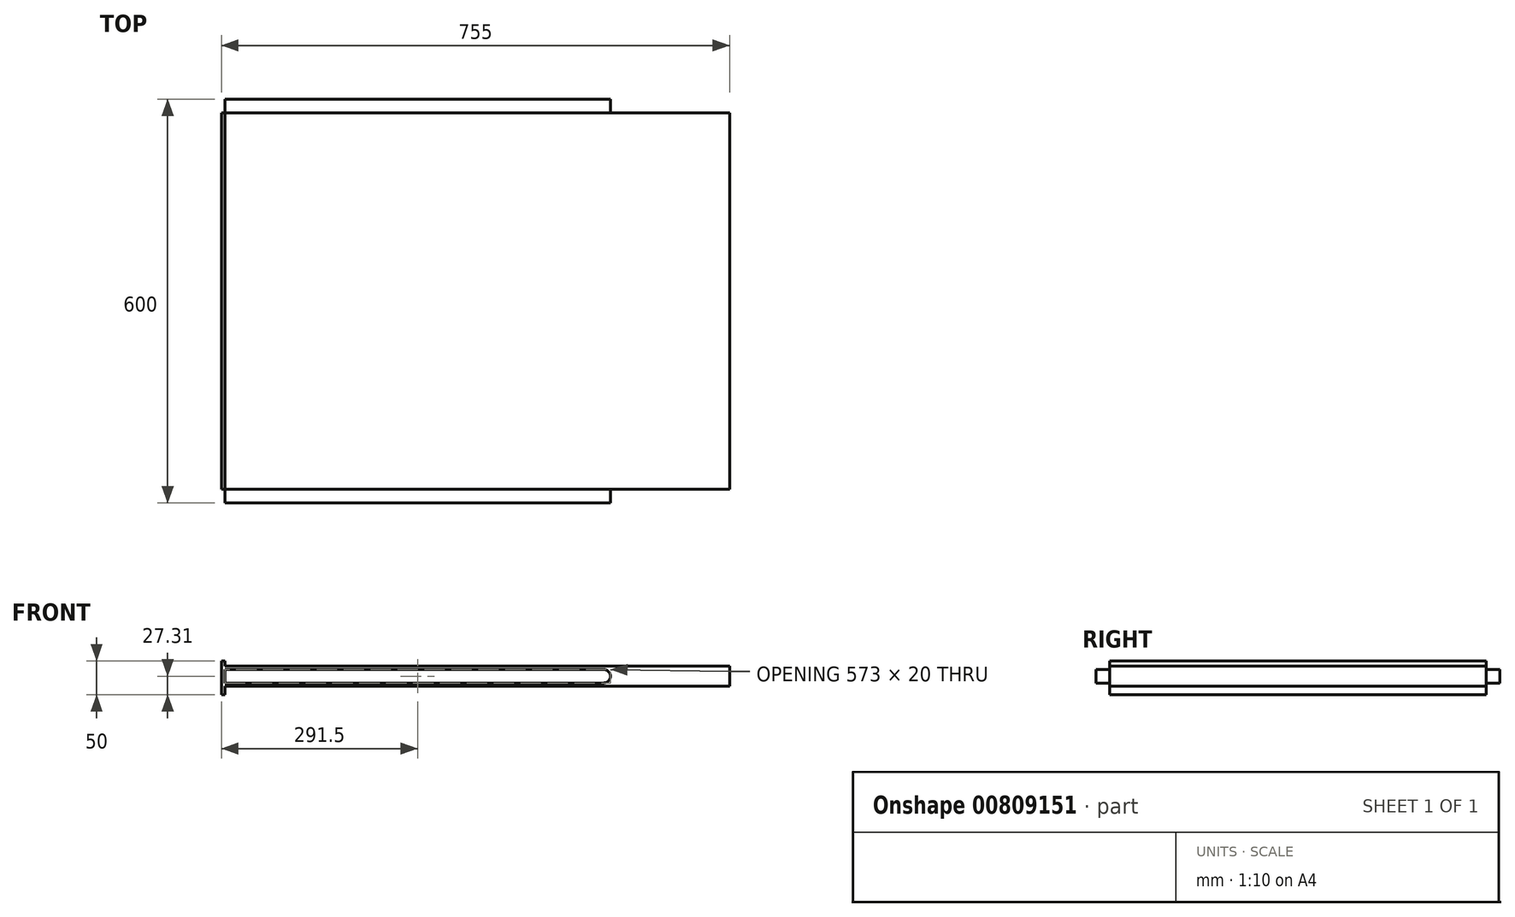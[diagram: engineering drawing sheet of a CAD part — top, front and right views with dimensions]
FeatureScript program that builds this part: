
annotation { "Feature Type Name" : "Feature", "Feature Type Description" : "" }
export const myFeature = defineFeature(function(context is Context, id is Id, definition is map)
    precondition{}
    {
        {
            var Q0;
            Q0=qCreatedBy(makeId("Top.planeOp"),FACE);
            var sketch = newSketch(context, id + "F0", { "sketchPlane" : qUnion([Q0])});
            skLineSegment(sketch, "E0.bottom", {"start": v(375, -280) * mm, "end": v(-375, -280) * mm});
            skLineSegment(sketch, "E0.top", {"start": v(375, 280) * mm, "end": v(-375, 280) * mm});
            skLineSegment(sketch, "E0.left", {"start": v(375, -280) * mm, "end": v(375, 280) * mm});
            skLineSegment(sketch, "E0.right", {"start": v(-375, -280) * mm, "end": v(-375, 280) * mm});
            skPoint(sketch, "E0.middle", {"position": v(0, 0) * mm});
            skSolve(sketch);
        }
        {
            var Q0;
            Q0 = qSketchRegion(id + "F0", true);
            extrude(context, id + "F1", {"entities" : qUnion([Q0]), "depth" : 30 * mm, "offsetDistance" : 25 * mm});
        }
        {
            var Q0;
            Q0=makeQuery(id+"F1.opExtrude","SWEPT_FACE",FACE,{"disambiguationData":[OSD([sQuery(id+"F0.wireOp",EDGE,"E0.bottom")])]});
            var sketch = newSketch(context, id + "F2", { "sketchPlane" : qUnion([Q0])});
            skLineSegment(sketch, "E1", {"start": v(-375, 5) * mm, "end": v(188, 5) * mm});
            skLineSegment(sketch, "E2", {"start": v(-375, 25) * mm, "end": v(188, 25) * mm});
            skArc(sketch, "E3", {"start": v(188, 25) * mm, "mid": v(198, 15) * mm, "end": v(188, 5) * mm});
            skSolve(sketch);
        }
        {
            var Q0;
            Q0=makeQuery(id+"F1.opExtrude","SWEPT_FACE",FACE,{"disambiguationData":[OSD([sQuery(id+"F0.wireOp",EDGE,"E0.top")])]});
            var sketch = newSketch(context, id + "F3", { "sketchPlane" : qUnion([Q0])});
            skLineSegment(sketch, "E4", {"start": v(375, 5) * mm, "end": v(-188, 5) * mm});
            skLineSegment(sketch, "E5", {"start": v(375, 25) * mm, "end": v(-188, 25) * mm});
            skArc(sketch, "E6", {"start": v(-188, 5) * mm, "mid": v(-198, 15) * mm, "end": v(-188, 25) * mm});
            skSolve(sketch);
        }
        {
            var Q0;
            {var subQ0=sQuery(id+"F3.wireOp",EDGE,"E4");Q0=makeQuery(id+"F3.imprint","IMPRINT",FACE,{"disambiguationData":[TD([[makeQuery(id+"F3.imprint","IMPRINT",EDGE,{"derivedFrom":subQ0}),-1.0]])]});}
            extrude(context, id + "F4", {"entities" : qUnion([Q0]), "operationType" : NewBodyOperationType.ADD, "depth" : 20 * mm, "offsetDistance" : 25 * mm});
        }
        {
            var Q0;
            {var subQ0=sQuery(id+"F2.wireOp",EDGE,"E1");Q0=makeQuery(id+"F2.imprint","IMPRINT",FACE,{"disambiguationData":[TD([[makeQuery(id+"F2.imprint","IMPRINT",EDGE,{"derivedFrom":subQ0}),1.0]])]});}
            extrude(context, id + "F5", {"entities" : qUnion([Q0]), "operationType" : NewBodyOperationType.ADD, "depth" : 20 * mm, "offsetDistance" : 25 * mm});
        }
        {
            var Q0;
            {var subQ0=sQuery(id+"F0.wireOp",EDGE,"E0.right");Q0=makeQuery(id+"F5.boolean.opBoolean","MERGE",FACE,{"derivedFrom":[makeQuery(id+"F4.boolean.opBoolean","MERGE",FACE,{"derivedFrom":[makeQuery(id+"F1.opExtrude","SWEPT_FACE",FACE,{"disambiguationData":[OSD([subQ0])]}),makeQuery(id+"F4.opExtrude","SWEPT_FACE",FACE,{"disambiguationData":[OSD([sQuery(id+"F0.wireOp",EDGE,"E0.top"),subQ0])]})]}),makeQuery(id+"F5.opExtrude","SWEPT_FACE",FACE,{"disambiguationData":[OSD([sQuery(id+"F0.wireOp",EDGE,"E0.bottom"),subQ0])]})]});}
            var sketch = newSketch(context, id + "F6", { "sketchPlane" : qUnion([Q0])});
            skLineSegment(sketch, "E7.bottom", {"start": v(280, -12.31) * mm, "end": v(-280, -12.31) * mm});
            skLineSegment(sketch, "E7.top", {"start": v(280, 37.69) * mm, "end": v(-280, 37.69) * mm});
            skLineSegment(sketch, "E7.left", {"start": v(280, -12.31) * mm, "end": v(280, 37.69) * mm});
            skLineSegment(sketch, "E7.right", {"start": v(-280, -12.31) * mm, "end": v(-280, 37.69) * mm});
            skPoint(sketch, "E7.middle", {"position": v(0, 12.69) * mm});
            skSolve(sketch);
        }
        {
            var Q0;
            Q0 = qSketchRegion(id + "F6", true);
            extrude(context, id + "F7", {"entities" : qUnion([Q0]), "operationType" : NewBodyOperationType.ADD, "depth" : 5 * mm, "offsetDistance" : 25 * mm});
        }
    });
